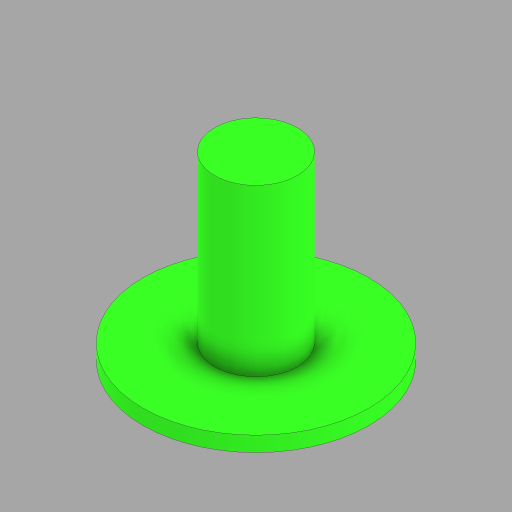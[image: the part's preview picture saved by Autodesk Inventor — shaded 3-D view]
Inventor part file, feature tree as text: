
AUTODESK INVENTOR PART (.ipt)
format: ipt  version: 2023 (Build 270158000, 158)  size: 116,224 bytes
history: native  units: mm
features: extrude x2, sketch x1
ambient origin geometry x8: Origin, YZ Plane, XZ Plane, XY Plane, X Axis, Y Axis, Z Axis, Center Point
bodies: Solid1 (feature_tree)
feature tree (3):
  sketch  "Sketch1"  dims[d0=15.0mm d1=5.5mm d2=1.0mm d3=0.0mm d4=12.0mm d5=0.0mm]
  extrude  "Extrusion1"  Depth=12.0mm
  extrude  "Extrusion2"  Depth=1.0mm TaperAngle=0.0deg
